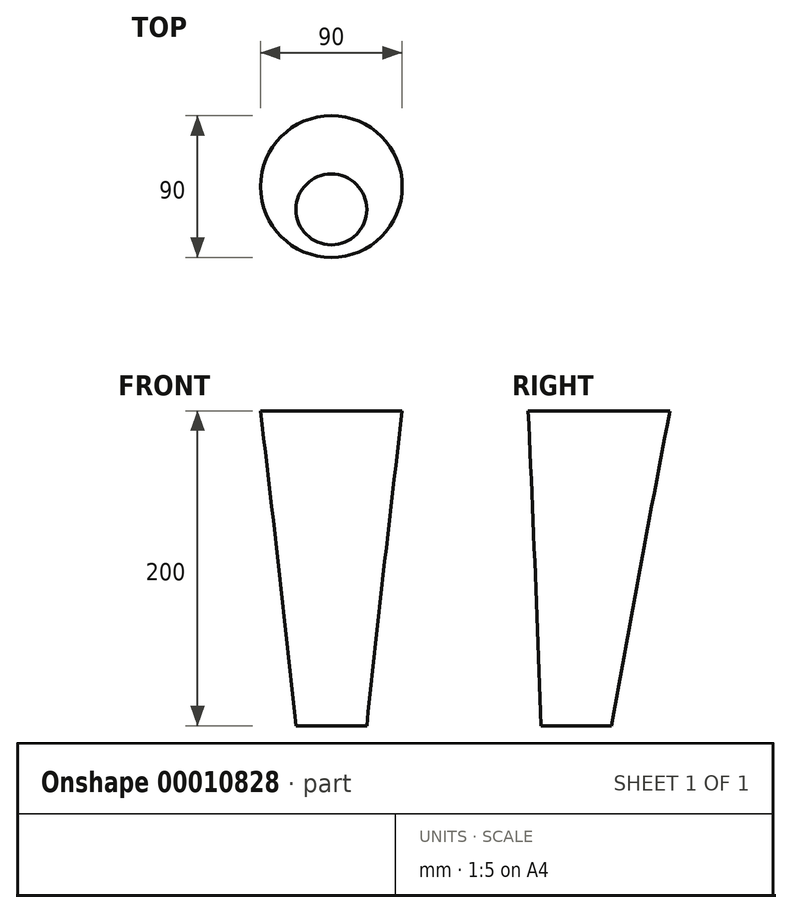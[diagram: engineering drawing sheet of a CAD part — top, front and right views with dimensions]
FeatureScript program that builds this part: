
annotation { "Feature Type Name" : "Feature", "Feature Type Description" : "" }
export const myFeature = defineFeature(function(context is Context, id is Id, definition is map)
    precondition{}
    {
        {
            var Q0;
            Q0=qCreatedBy(makeId("Top.planeOp"),FACE);
            var sketch = newSketch(context, id + "F0", { "sketchPlane" : qUnion([Q0])});
            skCircle(sketch, "E0", {"center": v(0, 0) * mm, "radius": 45 * mm});
            skSolve(sketch);
        }
        {
            var Q0;
            Q0=qCreatedBy(makeId("Top.planeOp"),FACE);
            cPlane(context, id + "F1", {"entities" : qUnion([Q0]), "cplaneType" : CPlaneType.OFFSET, "offset" : 200 * mm, "oppositeDirection" : true, "width" : 150 * mm, "height" : 150 * mm});
        }
        {
            var Q0;
            Q0=qCreatedBy(id+"F1.planeOp",FACE);
            var sketch = newSketch(context, id + "F2", { "sketchPlane" : qUnion([Q0])});
            skCircle(sketch, "E1", {"center": v(0, -14.52) * mm, "radius": 22.5 * mm});
            skSolve(sketch);
        }
        {
            var Q0;
            Q0=sQuery(id+"F0.wireOp",EDGE,"E0");
            var Q1;
            Q1=sQuery(id+"F2.wireOp",EDGE,"E1");
            loft(context, id + "F3", {"bodyType" : ToolBodyType.SURFACE, "wireProfilesArray" : [{ "wireProfileEntities" : qUnion([Q0]) }, { "wireProfileEntities" : qUnion([Q1]) }]});
        }
    });
